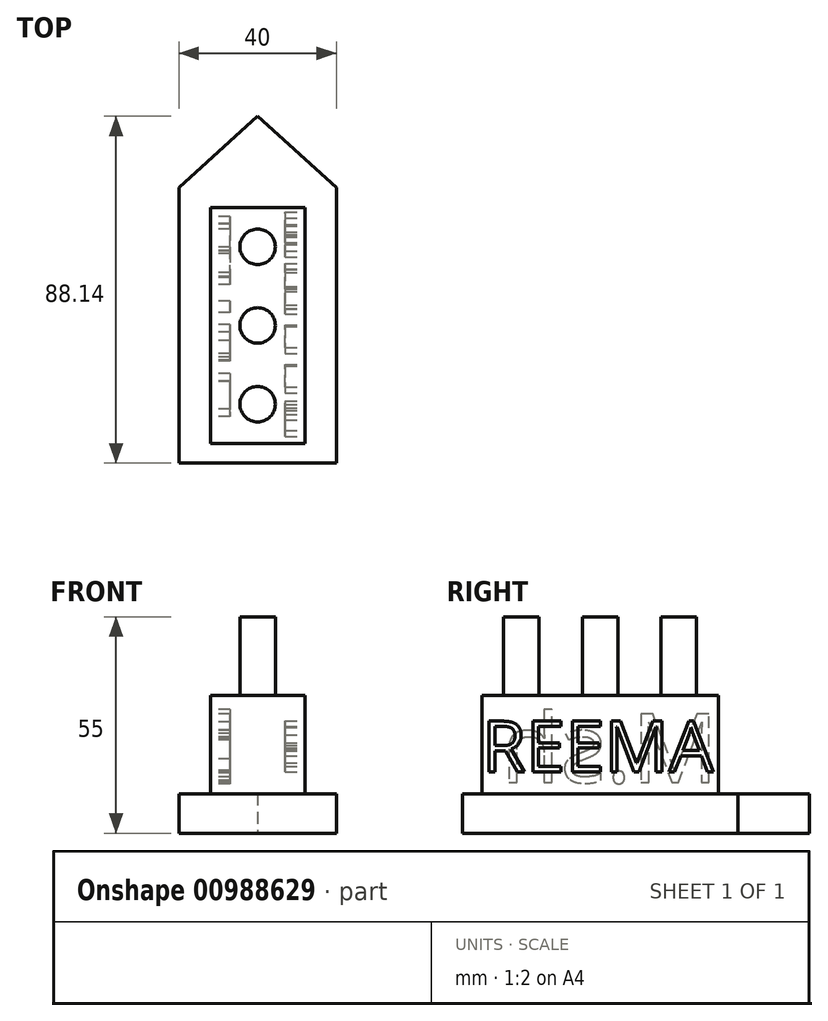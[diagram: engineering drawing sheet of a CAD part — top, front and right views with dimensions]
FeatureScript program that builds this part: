
annotation { "Feature Type Name" : "Feature", "Feature Type Description" : "" }
export const myFeature = defineFeature(function(context is Context, id is Id, definition is map)
    precondition{}
    {
        {
            var Q0;
            Q0=qCreatedBy(makeId("Top.planeOp"),FACE);
            var sketch = newSketch(context, id + "F0", { "sketchPlane" : qUnion([Q0])});
            skLineSegment(sketch, "E0", {"start": v(-20, -35) * mm, "end": v(-20, 35) * mm});
            skLineSegment(sketch, "E1", {"start": v(-20, 35) * mm, "end": v(0, 53.14) * mm});
            skLineSegment(sketch, "E2", {"start": v(20, -35) * mm, "end": v(20, 35) * mm});
            skLineSegment(sketch, "E3", {"start": v(20, 35) * mm, "end": v(0, 53.14) * mm});
            skLineSegment(sketch, "E4", {"start": v(-20, -35) * mm, "end": v(20, -35) * mm});
            skSolve(sketch);
        }
        {
            var Q0;
            Q0 = qSketchRegion(id + "F0", true);
            extrude(context, id + "F1", {"entities" : qUnion([Q0]), "depth" : 10 * mm, "offsetDistance" : 25 * mm});
        }
        {
            var Q0;
            Q0=makeQuery(id+"F1.opExtrude","CAP_FACE",FACE,{"disambiguationData":[OSD([sQuery(id+"F0.wireOp",EDGE,"E0"),sQuery(id+"F0.wireOp",EDGE,"E1"),sQuery(id+"F0.wireOp",EDGE,"E2"),sQuery(id+"F0.wireOp",EDGE,"E3"),sQuery(id+"F0.wireOp",EDGE,"E4")])],"isStart":false});
            var sketch = newSketch(context, id + "F2", { "sketchPlane" : qUnion([Q0])});
            skLineSegment(sketch, "E5", {"start": v(-12, 30) * mm, "end": v(-12, -30) * mm});
            skLineSegment(sketch, "E6", {"start": v(-12, -30) * mm, "end": v(12, -30) * mm});
            skLineSegment(sketch, "E7", {"start": v(-12, 30) * mm, "end": v(12, 30) * mm});
            skLineSegment(sketch, "E8", {"start": v(12, 30) * mm, "end": v(12, -30) * mm});
            skSolve(sketch);
        }
        {
            var Q0;
            Q0 = qSketchRegion(id + "F2", true);
            extrude(context, id + "F3", {"entities" : qUnion([Q0]), "operationType" : NewBodyOperationType.ADD, "depth" : 25 * mm, "offsetDistance" : 25 * mm});
        }
        {
            var Q0;
            Q0=makeQuery(id+"F3.opExtrude","CAP_FACE",FACE,{"disambiguationData":[OSD([sQuery(id+"F2.wireOp",EDGE,"E5"),sQuery(id+"F2.wireOp",EDGE,"E6"),sQuery(id+"F2.wireOp",EDGE,"E7"),sQuery(id+"F2.wireOp",EDGE,"E8")])],"isStart":false});
            var sketch = newSketch(context, id + "F4", { "sketchPlane" : qUnion([Q0])});
            skCircle(sketch, "E9", {"center": v(0, 0) * mm, "radius": 4.5 * mm});
            skCircle(sketch, "E10", {"center": v(0, 20) * mm, "radius": 4.5 * mm});
            skCircle(sketch, "E11", {"center": v(0, -20) * mm, "radius": 4.5 * mm});
            skSolve(sketch);
        }
        {
            var Q0;
            Q0 = qSketchRegion(id + "F4", true);
            extrude(context, id + "F5", {"entities" : qUnion([Q0]), "operationType" : NewBodyOperationType.ADD, "depth" : 20 * mm, "offsetDistance" : 25 * mm});
        }
        {
            var Q0;
            Q0=makeQuery(id+"F3.opExtrude","SWEPT_FACE",FACE,{"disambiguationData":[OSD([sQuery(id+"F2.wireOp",EDGE,"E5")])]});
            var sketch = newSketch(context, id + "F6", { "sketchPlane" : qUnion([Q0])});
            skText(sketch, "E12", { "text": "M.sh", "fontName": "OpenSans-Regular.ttf"});
            const initialGuessF6  = {"E12": [-0.03, 0.01289, 1, 0, 0.01756]};
            skSetInitialGuess(sketch, initialGuessF6);
            skSolve(sketch);
        }
        {
            var Q0;
            Q0=makeQuery(id+"F3.opExtrude","SWEPT_FACE",FACE,{"disambiguationData":[OSD([sQuery(id+"F2.wireOp",EDGE,"E8")])]});
            var sketch = newSketch(context, id + "F7", { "sketchPlane" : qUnion([Q0])});
            skText(sketch, "E13", { "text": "REEMA\n", "fontName": "OpenSans-Regular.ttf"});
            const initialGuessF7  = {"E13": [-0.03, 0.01561, 1, 0, 0.01297]};
            skSetInitialGuess(sketch, initialGuessF7);
            skSolve(sketch);
        }
        {
            var Q0;
            Q0 = qSketchRegion(id + "F6", true);
            extrude(context, id + "F8", {"entities" : qUnion([Q0]), "operationType" : NewBodyOperationType.REMOVE, "oppositeDirection" : true, "depth" : 5 * mm, "offsetDistance" : 25 * mm});
        }
        {
            var Q0;
            Q0 = qSketchRegion(id + "F7", true);
            extrude(context, id + "F9", {"entities" : qUnion([Q0]), "operationType" : NewBodyOperationType.REMOVE, "oppositeDirection" : true, "depth" : 5 * mm, "offsetDistance" : 25 * mm});
        }
    });
